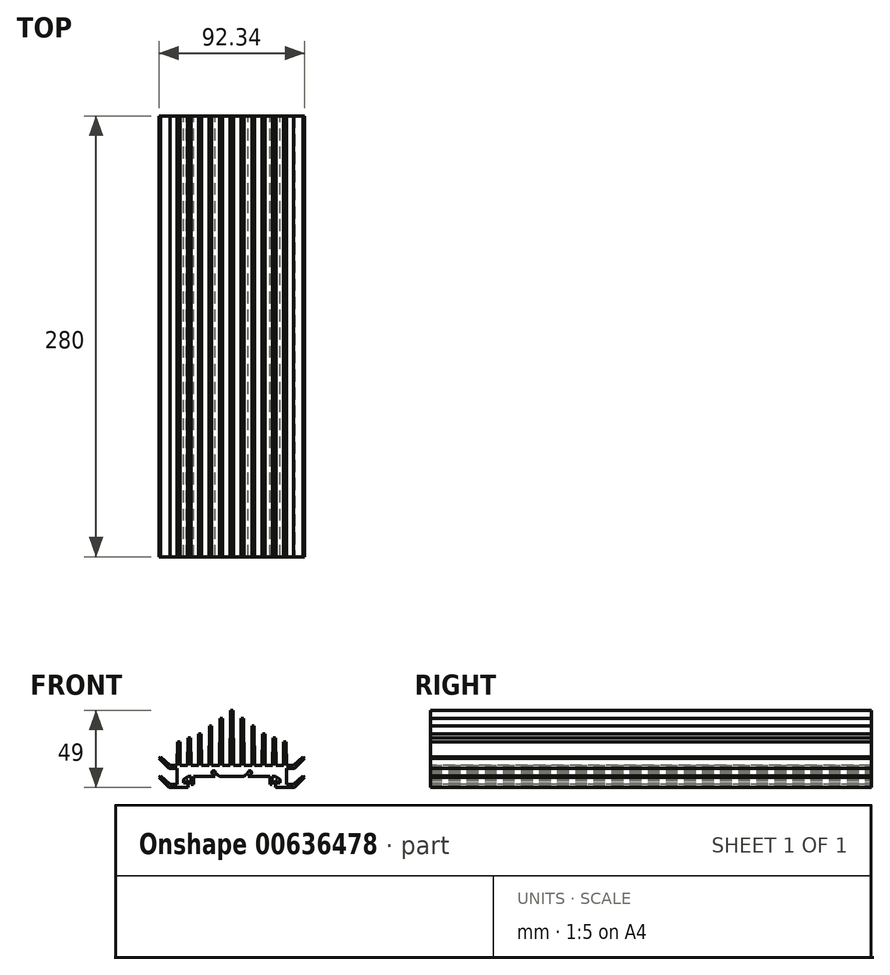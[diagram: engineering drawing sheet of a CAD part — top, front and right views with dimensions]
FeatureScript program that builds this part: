
annotation { "Feature Type Name" : "Feature", "Feature Type Description" : "" }
export const myFeature = defineFeature(function(context is Context, id is Id, definition is map)
    precondition{}
    {
        {
            var Q0;
            Q0=qCreatedBy(makeId("Front.planeOp"),FACE);
            var sketch = newSketch(context, id + "F0", { "sketchPlane" : qUnion([Q0])});
            skPoint(sketch, "E0.visualSharp", {"position": v(0, -3.5) * mm});
            skPoint(sketch, "E1.visualSharp", {"position": v(-32.75, 3.5) * mm});
            skLineSegment(sketch, "E2", {"start": v(-33, 18.5) * mm, "end": v(-34.5, 18.5) * mm});
            skLineSegment(sketch, "E3", {"start": v(-34.5, 18.5) * mm, "end": v(-34.72, 3.5) * mm});
            skLineSegment(sketch, "E4", {"start": v(-33, 18.5) * mm, "end": v(-32.75, 3.5) * mm});
            skLineSegment(sketch, "E5", {"start": v(-32.75, 3.5) * mm, "end": v(-28, 3.5) * mm});
            skLineSegment(sketch, "E6.1.0.0", {"start": v(-26.25, 21) * mm, "end": v(-26.01, 3.5) * mm});
            skLineSegment(sketch, "E6.1.0.2", {"start": v(-26.01, 3.5) * mm, "end": v(-21.24, 3.5) * mm});
            skPoint(sketch, "E6.1.0.3", {"position": v(-26.01, 3.5) * mm});
            skLineSegment(sketch, "E6.1.0.4", {"start": v(-26.25, 21) * mm, "end": v(-27.75, 21) * mm});
            skLineSegment(sketch, "E6.2.0.0", {"start": v(-19.5, 23.5) * mm, "end": v(-19.25, 3.5) * mm});
            skLineSegment(sketch, "E6.2.0.2", {"start": v(-19.25, 3.5) * mm, "end": v(-14.5, 3.5) * mm});
            skPoint(sketch, "E6.2.0.3", {"position": v(-19.25, 3.5) * mm});
            skLineSegment(sketch, "E6.2.0.4", {"start": v(-19.5, 23.5) * mm, "end": v(-21, 23.5) * mm});
            skLineSegment(sketch, "E6.3.0.0", {"start": v(-12.75, 28.5) * mm, "end": v(-12.75, 3.5) * mm});
            skLineSegment(sketch, "E6.3.0.2", {"start": v(-12.75, 3.5) * mm, "end": v(-7.75, 3.5) * mm});
            skPoint(sketch, "E6.3.0.3", {"position": v(-12.75, 3.5) * mm});
            skLineSegment(sketch, "E6.3.0.4", {"start": v(-12.75, 28.5) * mm, "end": v(-14.25, 28.5) * mm});
            skLineSegment(sketch, "E6.4.0.0", {"start": v(-6, 33.5) * mm, "end": v(-5.75, 3.5) * mm});
            skLineSegment(sketch, "E6.4.0.2", {"start": v(-5.75, 3.5) * mm, "end": v(-1, 3.5) * mm});
            skPoint(sketch, "E6.4.0.3", {"position": v(-5.75, 3.5) * mm});
            skLineSegment(sketch, "E6.4.0.4", {"start": v(-6, 33.5) * mm, "end": v(-7.5, 33.5) * mm});
            skLineSegment(sketch, "E6.5.0.4", {"start": v(0, 38.5) * mm, "end": v(-0.75, 38.5) * mm});
            skLineSegment(sketch, "E7", {"start": v(-27.75, 21) * mm, "end": v(-28, 3.5) * mm});
            skLineSegment(sketch, "E8", {"start": v(-21, 23.5) * mm, "end": v(-21.24, 3.5) * mm});
            skLineSegment(sketch, "E9", {"start": v(-0.75, 38.5) * mm, "end": v(-1, 3.5) * mm});
            skLineSegment(sketch, "E10", {"start": v(-7.75, 3.5) * mm, "end": v(-7.5, 33.5) * mm});
            skLineSegment(sketch, "E11", {"start": v(-14.25, 28.5) * mm, "end": v(-14.5, 3.5) * mm});
            skLineSegment(sketch, "E12", {"start": v(0, 38.5) * mm, "end": v(0, -3.5) * mm});
            skPoint(sketch, "E13", {"position": v(-34.72, 3.5) * mm});
            skLineSegment(sketch, "E14", {"start": v(0, -3.5) * mm, "end": v(-7.75, -3.5) * mm});
            skLineSegment(sketch, "E15", {"start": v(-34.72, 3.5) * mm, "end": v(-34.72, -10.5) * mm});
            skLineSegment(sketch, "E16", {"start": v(-7.75, -3.5) * mm, "end": v(-10.47, -1.22) * mm});
            skLineSegment(sketch, "E17", {"start": v(-10.47, -3.5) * mm, "end": v(-12.47, -1.82) * mm});
            skLineSegment(sketch, "E18", {"start": v(-12.47, -1.82) * mm, "end": v(-12.47, -0.82) * mm});
            skArc(sketch, "E19", {"start": v(-10.47, -0.82) * mm, "mid": v(-11.47, 0.18) * mm, "end": v(-12.47, -0.82) * mm});
            skLineSegment(sketch, "E20", {"start": v(-10.47, -0.82) * mm, "end": v(-10.47, -1.22) * mm});
            skLineSegment(sketch, "E21", {"start": v(-30.72, -7.47) * mm, "end": v(-28.72, -7.47) * mm});
            skLineSegment(sketch, "E22", {"start": v(-28.72, -7.47) * mm, "end": v(-28.72, -5.97) * mm});
            skLineSegment(sketch, "E23", {"start": v(-28.72, -5.97) * mm, "end": v(-27.72, -5.97) * mm});
            skLineSegment(sketch, "E24", {"start": v(-25.72, -3.5) * mm, "end": v(-25.72, -8.5) * mm});
            skLineSegment(sketch, "E25", {"start": v(-25.72, -8.5) * mm, "end": v(-24.22, -8.5) * mm});
            skLineSegment(sketch, "E26", {"start": v(-24.22, -8.5) * mm, "end": v(-24.22, -3.5) * mm});
            skLineSegment(sketch, "E27.trimOffspring", {"start": v(-24.22, -3.5) * mm, "end": v(-10.47, -3.5) * mm});
            skLineSegment(sketch, "E28", {"start": v(-25.72, -3.5) * mm, "end": v(-27.72, -3.5) * mm});
            skLineSegment(sketch, "E29", {"start": v(-34.72, -10.5) * mm, "end": v(-27.72, -10.5) * mm});
            skLineSegment(sketch, "E30", {"start": v(-27.72, -5.97) * mm, "end": v(-27.72, -10.5) * mm});
            skLineSegment(sketch, "E31", {"start": v(-27.72, -3.5) * mm, "end": v(-30.72, -5.23) * mm});
            skLineSegment(sketch, "E32", {"start": v(-30.72, -7.47) * mm, "end": v(-30.72, -5.23) * mm});
            skSolve(sketch);
        }
        {
            var Q0;
            Q0=qSketchRegion(id+"F0",true);
            extrude(context, id + "F1", {"entities" : qUnion([Q0]), "depth" : 280 * mm, "offsetDistance" : 25 * mm});
        }
        {
            var Q0;
            Q0=makeQuery(id+"F1.opExtrude","CAP_FACE",FACE,{"disambiguationData":[OSD([sQuery(id+"F0.wireOp",EDGE,"E2"),sQuery(id+"F0.wireOp",EDGE,"E3"),sQuery(id+"F0.wireOp",EDGE,"E4"),sQuery(id+"F0.wireOp",EDGE,"E5"),sQuery(id+"F0.wireOp",EDGE,"E6.1.0.0"),sQuery(id+"F0.wireOp",EDGE,"E6.1.0.2"),sQuery(id+"F0.wireOp",EDGE,"E6.1.0.4"),sQuery(id+"F0.wireOp",EDGE,"E6.2.0.0"),sQuery(id+"F0.wireOp",EDGE,"E6.2.0.2"),sQuery(id+"F0.wireOp",EDGE,"E6.2.0.4"),sQuery(id+"F0.wireOp",EDGE,"E6.3.0.0"),sQuery(id+"F0.wireOp",EDGE,"E6.3.0.2"),sQuery(id+"F0.wireOp",EDGE,"E6.3.0.4"),sQuery(id+"F0.wireOp",EDGE,"E6.4.0.0"),sQuery(id+"F0.wireOp",EDGE,"E6.4.0.2"),sQuery(id+"F0.wireOp",EDGE,"E6.4.0.4"),sQuery(id+"F0.wireOp",EDGE,"E6.5.0.4"),sQuery(id+"F0.wireOp",EDGE,"E7"),sQuery(id+"F0.wireOp",EDGE,"E8"),sQuery(id+"F0.wireOp",EDGE,"E9"),sQuery(id+"F0.wireOp",EDGE,"E10"),sQuery(id+"F0.wireOp",EDGE,"E11"),sQuery(id+"F0.wireOp",EDGE,"E12"),sQuery(id+"F0.wireOp",EDGE,"E14"),sQuery(id+"F0.wireOp",EDGE,"E15"),sQuery(id+"F0.wireOp",EDGE,"E16"),sQuery(id+"F0.wireOp",EDGE,"E17"),sQuery(id+"F0.wireOp",EDGE,"E18"),sQuery(id+"F0.wireOp",EDGE,"E19"),sQuery(id+"F0.wireOp",EDGE,"E20"),sQuery(id+"F0.wireOp",EDGE,"E21"),sQuery(id+"F0.wireOp",EDGE,"E22"),sQuery(id+"F0.wireOp",EDGE,"E23"),sQuery(id+"F0.wireOp",EDGE,"E24"),sQuery(id+"F0.wireOp",EDGE,"E25"),sQuery(id+"F0.wireOp",EDGE,"E26"),sQuery(id+"F0.wireOp",EDGE,"E27.trimOffspring"),sQuery(id+"F0.wireOp",EDGE,"E28"),sQuery(id+"F0.wireOp",EDGE,"E29"),sQuery(id+"F0.wireOp",EDGE,"E30"),sQuery(id+"F0.wireOp",EDGE,"E31"),sQuery(id+"F0.wireOp",EDGE,"E32")])],"isStart":false});
            var sketch = newSketch(context, id + "F2", { "sketchPlane" : qUnion([Q0])});
            skLineSegment(sketch, "E33", {"start": v(-34.72, -8.5) * mm, "end": v(-34.72, -10.5) * mm});
            skLineSegment(sketch, "E34", {"start": v(-39.22, -8.5) * mm, "end": v(-34.72, -8.5) * mm});
            skLineSegment(sketch, "E35", {"start": v(-39.72, -10.5) * mm, "end": v(-34.72, -10.5) * mm});
            skPoint(sketch, "E36", {"position": v(-45.11, -2.99) * mm});
            skLineSegment(sketch, "E37", {"start": v(-39.22, -8.5) * mm, "end": v(-45.11, -2.99) * mm});
            skPoint(sketch, "E38", {"position": v(-46.17, -4.05) * mm});
            skLineSegment(sketch, "E39", {"start": v(-39.72, -10.5) * mm, "end": v(-46.17, -4.05) * mm});
            skLineSegment(sketch, "E40", {"start": v(-46.17, -4.05) * mm, "end": v(-45.11, -2.99) * mm});
            skPoint(sketch, "E41.0.1.0", {"position": v(-45.11, 9.01) * mm});
            skPoint(sketch, "E41.0.1.1", {"position": v(-46.17, 7.95) * mm});
            skLineSegment(sketch, "E41.0.1.2", {"start": v(-39.72, 1.5) * mm, "end": v(-34.72, 1.5) * mm});
            skLineSegment(sketch, "E41.0.1.3", {"start": v(-34.72, 3.5) * mm, "end": v(-34.72, 1.5) * mm});
            skLineSegment(sketch, "E41.0.1.4", {"start": v(-39.22, 3.5) * mm, "end": v(-34.72, 3.5) * mm});
            skLineSegment(sketch, "E41.0.1.5", {"start": v(-39.72, 1.5) * mm, "end": v(-46.17, 7.95) * mm});
            skLineSegment(sketch, "E41.0.1.6", {"start": v(-39.22, 3.5) * mm, "end": v(-45.11, 9.01) * mm});
            skLineSegment(sketch, "E41.0.1.7", {"start": v(-46.17, 7.95) * mm, "end": v(-45.11, 9.01) * mm});
            skLineSegment(sketch, "E41.direction1", {"start": v(-39.72, -10.5) * mm, "end": v(-14.72, -10.5) * mm, "construction": true});
            skLineSegment(sketch, "E41.direction2", {"start": v(-39.72, -10.5) * mm, "end": v(-39.72, 1.5) * mm, "construction": true});
            skSolve(sketch);
        }
        {
            var Q0;
            Q0 = qSketchRegion(id + "F2", true);
            extrude(context, id + "F3", {"entities" : qUnion([Q0]), "operationType" : NewBodyOperationType.ADD, "oppositeDirection" : true, "depth" : 280 * mm, "offsetDistance" : 25 * mm});
        }
        {
            var Q0;
            Q0=makeQuery(id+"F1.opExtrude","SWEPT_BODY",BODY,{"disambiguationData":[OSD([sQuery(id+"F0.wireOp",EDGE,"TnubSqON-79KH-nLpW-ZS85-RthiU6LkHpQQ"),sQuery(id+"F0.wireOp",EDGE,"d4040ae1-49fa-467b-b834-68955a7aff6c.filletArc"),sQuery(id+"F0.wireOp",EDGE,"0p0NX7ig-sMd9-ppPj-pS5j-73VNfbG47QIz"),sQuery(id+"F0.wireOp",EDGE,"hHlwevkY-eqD7-Qv4w-a98q-xilTCphLJCeT.bottom"),sQuery(id+"F0.wireOp",EDGE,"6x9CJkuz-Tdnq-FKfW-2rxk-apdPEEXZA9Xt"),sQuery(id+"F0.wireOp",EDGE,"u6GS7FUT-5I9F-KbIJ-NuOU-u1geYBGq60Gm"),sQuery(id+"F0.wireOp",EDGE,"E2"),sQuery(id+"F0.wireOp",EDGE,"E3"),sQuery(id+"F0.wireOp",EDGE,"E4"),sQuery(id+"F0.wireOp",EDGE,"E5"),sQuery(id+"F0.wireOp",EDGE,"E6.1.0.0"),sQuery(id+"F0.wireOp",EDGE,"E6.1.0.2"),sQuery(id+"F0.wireOp",EDGE,"E6.1.0.4"),sQuery(id+"F0.wireOp",EDGE,"E6.2.0.0"),sQuery(id+"F0.wireOp",EDGE,"E6.2.0.2"),sQuery(id+"F0.wireOp",EDGE,"E6.2.0.4"),sQuery(id+"F0.wireOp",EDGE,"E6.3.0.0"),sQuery(id+"F0.wireOp",EDGE,"E6.3.0.2"),sQuery(id+"F0.wireOp",EDGE,"E6.3.0.4"),sQuery(id+"F0.wireOp",EDGE,"E6.4.0.0"),sQuery(id+"F0.wireOp",EDGE,"E6.4.0.2"),sQuery(id+"F0.wireOp",EDGE,"E6.4.0.4"),sQuery(id+"F0.wireOp",EDGE,"E6.5.0.4"),sQuery(id+"F0.wireOp",EDGE,"E7"),sQuery(id+"F0.wireOp",EDGE,"E8"),sQuery(id+"F0.wireOp",EDGE,"E9"),sQuery(id+"F0.wireOp",EDGE,"E10"),sQuery(id+"F0.wireOp",EDGE,"E11"),sQuery(id+"F0.wireOp",EDGE,"E12"),sQuery(id+"F0.wireOp",EDGE,"e99ae112-1fcd-4d8d-b843-6319c6136938.filletArc"),sQuery(id+"F0.wireOp",EDGE,"dpcpTgc0-tMbv-GZai-5xlN-lojXniI1dxTx"),sQuery(id+"F0.wireOp",EDGE,"r8P8cLXi-dr0I-Mbf4-CPRH-vQ3sMQNvhFXj"),sQuery(id+"F0.wireOp",EDGE,"ucv5H1sf-fYlp-sK0K-A0lg-dWywTaSMHclT"),sQuery(id+"F0.wireOp",EDGE,"8KMzuQ8W-cXxm-lNf7-nVmo-U00ck15BO8Df"),sQuery(id+"F0.wireOp",EDGE,"94e2b7ff-8018-4e68-97f3-c9f3518b66d6.trimOffspring")])]});
            var Q1;
            Q1=makeQuery(id+"F1.opExtrude","SWEPT_FACE",FACE,{"disambiguationData":[OSD([sQuery(id+"F0.wireOp",EDGE,"E12")])]});
            mirror(context, id + "F4", {"operationType" : NewBodyOperationType.ADD, "entities" : qUnion([Q0]), "mirrorPlane" : qUnion([Q1])});
        }
    });
